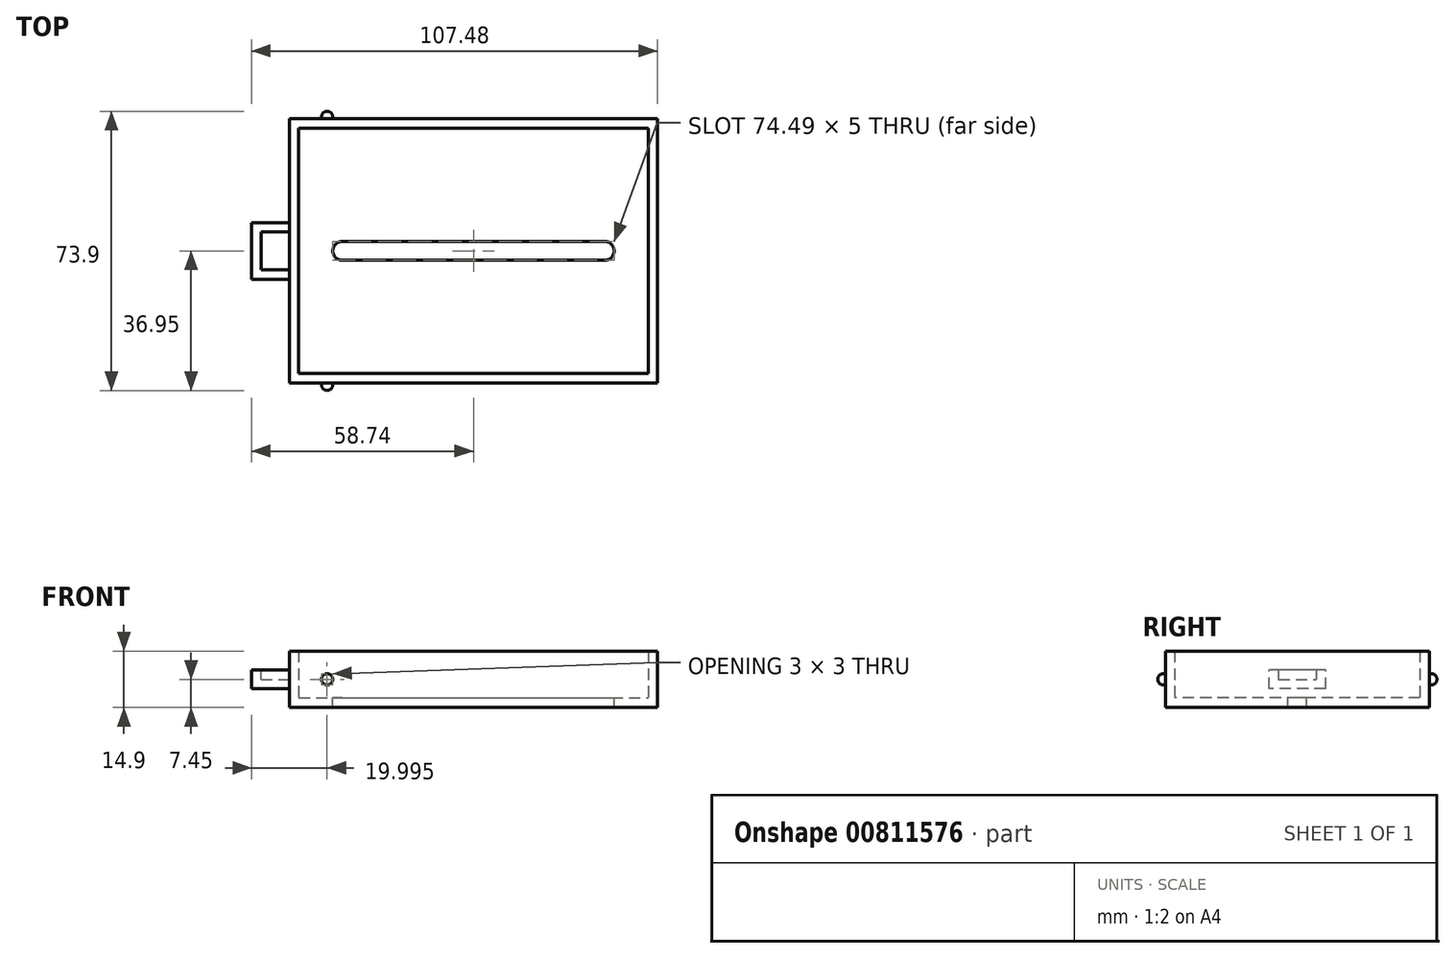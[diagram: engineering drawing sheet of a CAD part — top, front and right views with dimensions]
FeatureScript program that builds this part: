
annotation { "Feature Type Name" : "Feature", "Feature Type Description" : "" }
export const myFeature = defineFeature(function(context is Context, id is Id, definition is map)
    precondition{}
    {
        {
            var Q0;
            Q0=qCreatedBy(makeId("Top.planeOp"),FACE);
            var sketch = newSketch(context, id + "F0", { "sketchPlane" : qUnion([Q0])});
            skLineSegment(sketch, "E0.bottom", {"start": v(-48.74, 34.95) * mm, "end": v(48.75, 34.95) * mm});
            skLineSegment(sketch, "E0.top", {"start": v(-48.75, -34.95) * mm, "end": v(48.74, -34.95) * mm});
            skLineSegment(sketch, "E0.left", {"start": v(-48.74, 34.95) * mm, "end": v(-48.75, -34.95) * mm});
            skLineSegment(sketch, "E0.right", {"start": v(48.75, 34.95) * mm, "end": v(48.74, -34.95) * mm});
            skPoint(sketch, "E0.middle", {"position": v(0, 0) * mm});
            skSolve(sketch);
        }
        {
            var Q0;
            Q0=makeQuery(id+"F0.imprint","IMPRINT",FACE,{"disambiguationData":[TD([[makeQuery(id+"F0.imprint","IMPRINT",EDGE,{"derivedFrom":sQuery(id+"F0.wireOp",EDGE,"E0.bottom")}),-1.0]])]});
            extrude(context, id + "F1", {"entities" : qUnion([Q0]), "depth" : 14.9 * mm, "offsetDistance" : 25 * mm});
        }
        {
            var Q0;
            Q0=makeQuery(id+"F1.opExtrude","CAP_FACE",FACE,{"disambiguationData":[OSD([sQuery(id+"F0.wireOp",EDGE,"E0.bottom"),sQuery(id+"F0.wireOp",EDGE,"E0.top"),sQuery(id+"F0.wireOp",EDGE,"E0.left"),sQuery(id+"F0.wireOp",EDGE,"E0.right")])],"isStart":false});
            shell(context, id + "F2", {"entities" : qUnion([Q0]), "thickness" : 2.5 * mm});
        }
        {
            var Q0;
            Q0=makeQuery(id+"F1.opExtrude","SWEPT_FACE",FACE,{"disambiguationData":[OSD([sQuery(id+"F0.wireOp",EDGE,"E0.left")])]});
            var sketch = newSketch(context, id + "F3", { "sketchPlane" : qUnion([Q0])});
            skLineSegment(sketch, "E1.bottom", {"start": v(-7.5, 4.95) * mm, "end": v(7.5, 4.95) * mm});
            skLineSegment(sketch, "E1.top", {"start": v(-7.5, 9.95) * mm, "end": v(7.5, 9.95) * mm});
            skLineSegment(sketch, "E1.left", {"start": v(-7.5, 4.95) * mm, "end": v(-7.5, 9.95) * mm});
            skLineSegment(sketch, "E1.right", {"start": v(7.5, 4.95) * mm, "end": v(7.5, 9.95) * mm});
            skPoint(sketch, "E1.middle", {"position": v(0, 7.45) * mm});
            skLineSegment(sketch, "E2", {"start": v(0, 9.95) * mm, "end": v(0, 14.9) * mm});
            skLineSegment(sketch, "E3", {"start": v(0, 4.95) * mm, "end": v(0, 0) * mm});
            skSolve(sketch);
        }
        {
            var Q0;
            {var subQ3=sQuery(id+"F3.wireOp",EDGE,"E1.left");Q0=makeQuery(id+"F3.imprint","IMPRINT",FACE,{"disambiguationData":[TD([[makeQuery(id+"F3.imprint","IMPRINT",EDGE,{"derivedFrom":subQ3}),-1.0]])]});}
            extrude(context, id + "F4", {"entities" : qUnion([Q0]), "operationType" : NewBodyOperationType.ADD, "depth" : 10 * mm, "offsetDistance" : 25 * mm});
        }
        {
            var Q0;
            Q0=makeQuery(id+"F4.opExtrude","SWEPT_FACE",FACE,{"disambiguationData":[OSD([sQuery(id+"F3.wireOp",EDGE,"E1.top")])]});
            shell(context, id + "F5", {"entities" : qUnion([Q0]), "thickness" : 2.5 * mm});
        }
        {
            var Q0;
            Q0=makeQuery(id+"F1.opExtrude","SWEPT_FACE",FACE,{"disambiguationData":[OSD([sQuery(id+"F0.wireOp",EDGE,"E0.bottom")])]});
            var sketch = newSketch(context, id + "F6", { "sketchPlane" : qUnion([Q0])});
            skPoint(sketch, "E4", {"position": v(38.74, 7.45) * mm});
            skPoint(sketch, "E4.positionSnap0", {"position": v(48.74, 7.45) * mm});
            skCircle(sketch, "E5", {"center": v(38.74, 7.45) * mm, "radius": 1.5 * mm});
            skSolve(sketch);
        }
        {
            var Q0;
            Q0=makeQuery(id+"F6.imprint","IMPRINT",FACE,{"disambiguationData":[TD([[makeQuery(id+"F6.imprint","IMPRINT",EDGE,{"derivedFrom":sQuery(id+"F6.wireOp",EDGE,"E5")}),1.0]])]});
            extrude(context, id + "F7", {"entities" : qUnion([Q0]), "operationType" : NewBodyOperationType.ADD, "depth" : 2 * mm, "offsetDistance" : 25 * mm});
        }
        {
            var Q0;
            Q0=makeQuery(id+"F7.opExtrude","CAP_FACE",FACE,{"disambiguationData":[OSD([sQuery(id+"F6.wireOp",EDGE,"E5")])],"isStart":false});
            fillet(context, id + "F8", {"entities" : qUnion([Q0]), "radius" : 1.5 * mm, "tangentPropagation" : true, "allowEdgeOverflow" : false});
        }
        {
            var Q0;
            Q0=makeQuery(id+"F1.opExtrude","SWEPT_FACE",FACE,{"disambiguationData":[OSD([sQuery(id+"F0.wireOp",EDGE,"E0.top")])]});
            var sketch = newSketch(context, id + "F9", { "sketchPlane" : qUnion([Q0])});
            skPoint(sketch, "E6", {"position": v(-38.75, 7.45) * mm});
            skPoint(sketch, "E6.positionSnap0", {"position": v(-48.75, 7.45) * mm});
            skCircle(sketch, "E7", {"center": v(-38.75, 7.45) * mm, "radius": 1.5 * mm});
            skSolve(sketch);
        }
        {
            var Q0;
            Q0=makeQuery(id+"F9.imprint","IMPRINT",FACE,{"disambiguationData":[TD([[makeQuery(id+"F9.imprint","IMPRINT",EDGE,{"derivedFrom":sQuery(id+"F9.wireOp",EDGE,"E7")}),1.0]])]});
            extrude(context, id + "F10", {"entities" : qUnion([Q0]), "operationType" : NewBodyOperationType.ADD, "depth" : 2 * mm, "offsetDistance" : 25 * mm});
        }
        {
            var Q0;
            Q0=makeQuery(id+"F10.opExtrude","CAP_FACE",FACE,{"disambiguationData":[OSD([sQuery(id+"F9.wireOp",EDGE,"E7")])],"isStart":false});
            fillet(context, id + "F11", {"entities" : qUnion([Q0]), "radius" : 1.5 * mm, "tangentPropagation" : true, "allowEdgeOverflow" : false});
        }
        {
            var Q0;
            Q0=makeQuery(id+"F2.opShell","OFFSET_FACE",FACE,{"disambiguationData":[OSD([sQuery(id+"F0.wireOp",EDGE,"E0.bottom"),sQuery(id+"F0.wireOp",EDGE,"E0.top"),sQuery(id+"F0.wireOp",EDGE,"E0.left"),sQuery(id+"F0.wireOp",EDGE,"E0.right")])]});
            var sketch = newSketch(context, id + "F12", { "sketchPlane" : qUnion([Q0])});
            skLineSegment(sketch, "E8", {"start": v(-46.25, 0) * mm, "end": v(-37.24, 0) * mm});
            skLineSegment(sketch, "E9", {"start": v(46.25, 0) * mm, "end": v(37.24, 0) * mm});
            skLineSegment(sketch, "E10.bottom", {"start": v(-37.24, -2.5) * mm, "end": v(37.24, -2.5) * mm});
            skLineSegment(sketch, "E10.top", {"start": v(-37.24, 2.5) * mm, "end": v(37.24, 2.5) * mm});
            skLineSegment(sketch, "E10.left", {"start": v(-37.24, -2.5) * mm, "end": v(-37.24, 2.5) * mm});
            skLineSegment(sketch, "E10.right", {"start": v(37.24, -2.5) * mm, "end": v(37.24, 2.5) * mm});
            skPoint(sketch, "E10.middle", {"position": v(0, 0) * mm});
            skCircle(sketch, "E11", {"center": v(-34.74, 0) * mm, "radius": 2.5 * mm});
            skCircle(sketch, "E12", {"center": v(34.74, 0) * mm, "radius": 2.5 * mm});
            skSolve(sketch);
        }
        {
            var Q0;
            {var subQ0=sQuery(id+"F12.wireOp",EDGE,"E11");var subQ1=sQuery(id+"F12.wireOp",EDGE,"E10.bottom");var subQ2=makeQuery(id+"F12.imprint","INTERSECT",VERTEX,{"derivedFrom":[subQ1,subQ0]});Q0=makeQuery(id+"F12.imprint","IMPRINT",FACE,{"disambiguationData":[TD([[makeQuery(id+"F12.imprint","IMPRINT",EDGE,{"disambiguationData":[TD([[subQ2,-1.0]])],"derivedFrom":subQ1}),1.0]])]});}
            extrude(context, id + "F13", {"entities" : qUnion([Q0]), "operationType" : NewBodyOperationType.REMOVE, "oppositeDirection" : true, "depth" : 25 * mm, "offsetDistance" : 25 * mm});
        }
        {
            var Q0;
            {var subQ0=sQuery(id+"F12.wireOp",EDGE,"E11");var subQ3=makeQuery(id+"F12.imprint","INTERSECT",VERTEX,{"derivedFrom":[sQuery(id+"F12.wireOp",EDGE,"E10.bottom"),subQ0]});Q0=makeQuery(id+"F12.imprint","IMPRINT",FACE,{"disambiguationData":[TD([[makeQuery(id+"F12.imprint","IMPRINT",EDGE,{"disambiguationData":[TD([[subQ3,-1.0]])],"derivedFrom":subQ0}),1.0]])]});}
            var Q1;
            {var subQ0=sQuery(id+"F12.wireOp",EDGE,"E12");var subQ3=makeQuery(id+"F12.imprint","INTERSECT",VERTEX,{"derivedFrom":[sQuery(id+"F12.wireOp",EDGE,"E10.bottom"),subQ0]});Q1=makeQuery(id+"F12.imprint","IMPRINT",FACE,{"disambiguationData":[TD([[makeQuery(id+"F12.imprint","IMPRINT",EDGE,{"disambiguationData":[TD([[subQ3,1.0]])],"derivedFrom":subQ0}),1.0]])]});}
            extrude(context, id + "F14", {"entities" : qUnion([Q0, Q1]), "operationType" : NewBodyOperationType.REMOVE, "oppositeDirection" : true, "depth" : 25 * mm, "offsetDistance" : 25 * mm});
        }
    });
